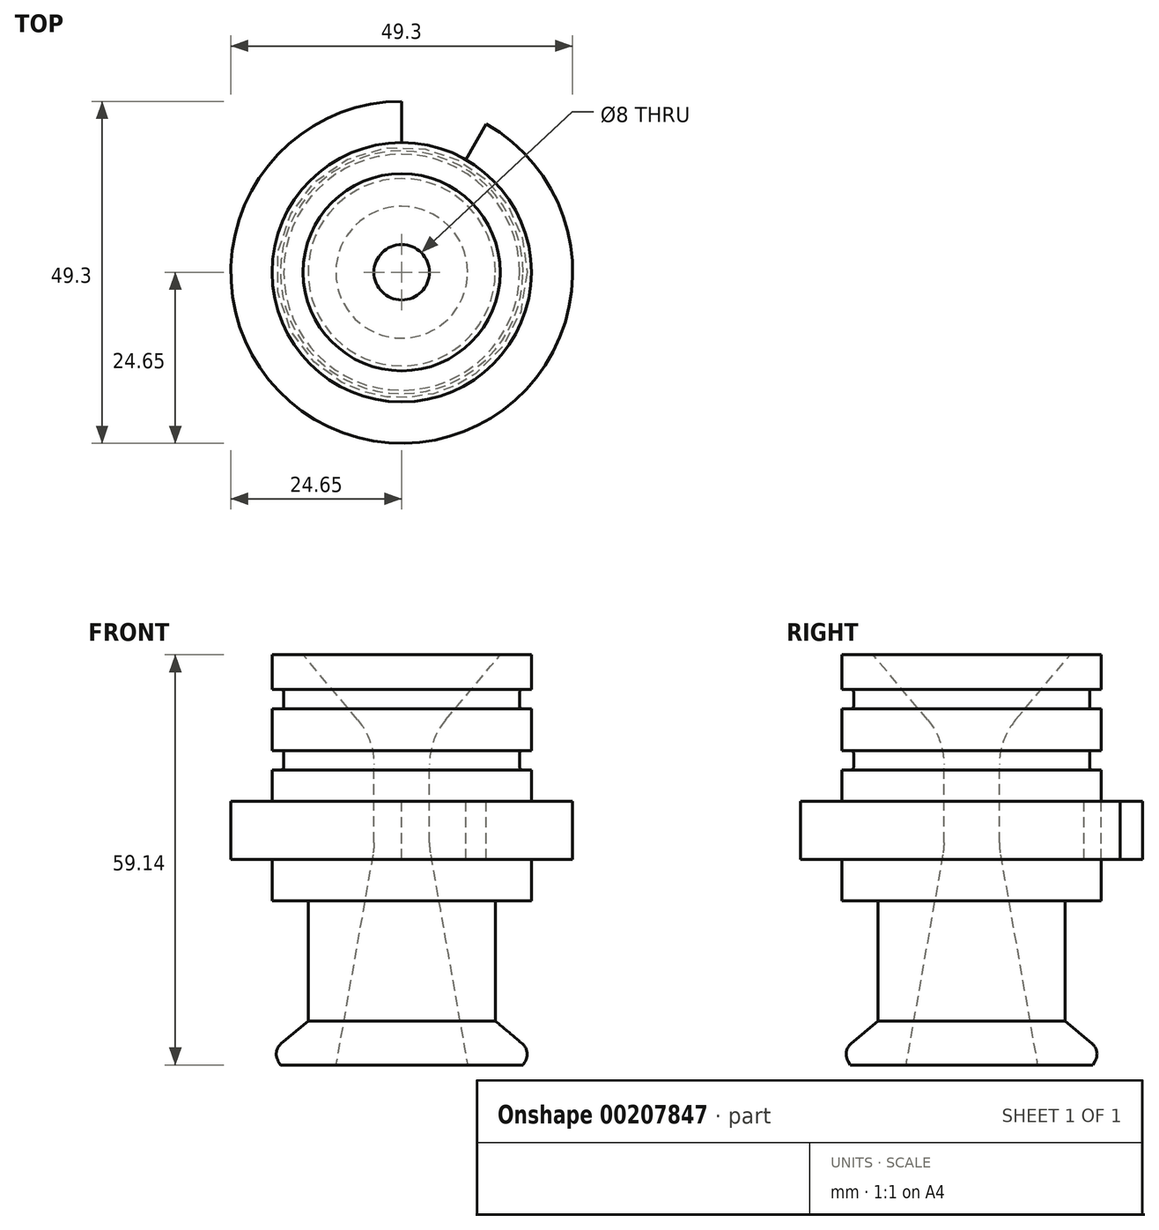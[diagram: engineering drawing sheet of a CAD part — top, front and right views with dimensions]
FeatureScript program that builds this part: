
annotation { "Feature Type Name" : "Feature", "Feature Type Description" : "" }
export const myFeature = defineFeature(function(context is Context, id is Id, definition is map)
    precondition{}
    {
        {
            var Q0;
            Q0=qCreatedBy(makeId("Front.planeOp"),FACE);
            var sketch = newSketch(context, id + "F0", { "sketchPlane" : qUnion([Q0])});
            skLineSegment(sketch, "E0", {"start": v(-18.7, 0) * mm, "end": v(-18.7, 6) * mm});
            skLineSegment(sketch, "E1", {"start": v(-18.7, 6) * mm, "end": v(-24.65, 6) * mm});
            skLineSegment(sketch, "E2", {"start": v(-24.65, 6) * mm, "end": v(-24.65, 14.4) * mm});
            skLineSegment(sketch, "E3", {"start": v(-18.7, 14.4) * mm, "end": v(-18.7, 18.9) * mm});
            skLineSegment(sketch, "E4", {"start": v(-18.7, 18.9) * mm, "end": v(-17.42, 18.9) * mm});
            skLineSegment(sketch, "E5", {"start": v(-17.02, 19.3) * mm, "end": v(-17.02, 21.3) * mm});
            skLineSegment(sketch, "E6", {"start": v(-17.42, 21.7) * mm, "end": v(-18.7, 21.7) * mm});
            skLineSegment(sketch, "E7", {"start": v(-18.7, 21.7) * mm, "end": v(-18.7, 27.7) * mm});
            skLineSegment(sketch, "E8", {"start": v(-18.7, 27.7) * mm, "end": v(-17.42, 27.7) * mm});
            skLineSegment(sketch, "E9", {"start": v(-17.02, 28.1) * mm, "end": v(-17.02, 30.1) * mm});
            skLineSegment(sketch, "E10", {"start": v(-17.42, 30.5) * mm, "end": v(-18.7, 30.5) * mm});
            skLineSegment(sketch, "E11", {"start": v(-18.7, 14.4) * mm, "end": v(-24.65, 14.4) * mm});
            skLineSegment(sketch, "E12", {"start": v(-14.22, 35.5) * mm, "end": v(-6.34, 26.11) * mm});
            skLineSegment(sketch, "E13", {"start": v(-4, 8.43) * mm, "end": v(-4, 19.68) * mm});
            skLineSegment(sketch, "E14", {"start": v(0, 48.19) * mm, "end": v(0, -42.57) * mm});
            skPoint(sketch, "E15.visualSharp", {"position": v(-4, 23.32) * mm});
            skArc(sketch, "E15.filletArc", {"start": v(-4, 19.68) * mm, "mid": v(-4.6, 23.1) * mm, "end": v(-6.34, 26.11) * mm});
            skPoint(sketch, "E16.visualSharp", {"position": v(-4, 7.32) * mm});
            skArc(sketch, "E16.filletArc", {"start": v(-4.15, 6.7) * mm, "mid": v(-4.04, 7.55) * mm, "end": v(-4, 8.43) * mm});
            skLineSegment(sketch, "E17", {"start": v(-18.7, 30.5) * mm, "end": v(-18.7, 35.5) * mm});
            skLineSegment(sketch, "E18", {"start": v(-18.7, 35.5) * mm, "end": v(-14.22, 35.5) * mm});
            skLineSegment(sketch, "E19", {"start": v(-4.15, 6.7) * mm, "end": v(-9.5, -23.64) * mm});
            skLineSegment(sketch, "E20", {"start": v(-13.5, 0) * mm, "end": v(-18.7, 0) * mm});
            skLineSegment(sketch, "E21", {"start": v(-17.5, -23.64) * mm, "end": v(-9.5, -23.64) * mm});
            skLineSegment(sketch, "E22", {"start": v(-17.5, -23.64) * mm, "end": v(-17.82, -23.08) * mm});
            skLineSegment(sketch, "E23", {"start": v(-17.38, -20.55) * mm, "end": v(-13.5, -17.3) * mm});
            skPoint(sketch, "E24.visualSharp", {"position": v(-18.66, -21.63) * mm});
            skArc(sketch, "E24.filletArc", {"start": v(-17.38, -20.55) * mm, "mid": v(-18.06, -21.74) * mm, "end": v(-17.82, -23.08) * mm});
            skLineSegment(sketch, "E25", {"start": v(-13.5, 0) * mm, "end": v(-13.5, -17.3) * mm});
            skPoint(sketch, "E26.visualSharp", {"position": v(-17.02, 30.5) * mm});
            skArc(sketch, "E26.filletArc", {"start": v(-17.02, 30.1) * mm, "mid": v(-17.14, 30.38) * mm, "end": v(-17.42, 30.5) * mm});
            skPoint(sketch, "E27.visualSharp", {"position": v(-17.02, 27.7) * mm});
            skArc(sketch, "E27.filletArc", {"start": v(-17.42, 27.7) * mm, "mid": v(-17.14, 27.82) * mm, "end": v(-17.02, 28.1) * mm});
            skPoint(sketch, "E28.visualSharp", {"position": v(-17.02, 21.7) * mm});
            skArc(sketch, "E28.filletArc", {"start": v(-17.02, 21.3) * mm, "mid": v(-17.14, 21.58) * mm, "end": v(-17.42, 21.7) * mm});
            skPoint(sketch, "E29.visualSharp", {"position": v(-17.02, 18.9) * mm});
            skArc(sketch, "E29.filletArc", {"start": v(-17.42, 18.9) * mm, "mid": v(-17.14, 19.02) * mm, "end": v(-17.02, 19.3) * mm});
            skSolve(sketch);
        }
        {
            var Q0;
            Q0=qSketchRegion(id+"F0",true);
            var Q1;
            Q1=sQuery(id+"F0.wireOp",EDGE,"E14");
            revolve(context, id + "F1", {"entities" : qUnion([Q0]), "axis" : qUnion([Q1]), "revolveType" : RevolveType.FULL});
        }
        {
            var Q0;
            Q0=makeQuery(id+"F1.opRevolve","SWEPT_FACE",FACE,{"disambiguationData":[OSD([sQuery(id+"F0.wireOp",EDGE,"E11")])]});
            var sketch = newSketch(context, id + "F2", { "sketchPlane" : qUnion([Q0])});
            skCircle(sketch, "E30.cCircle", {"center": v(0, 0) * mm, "radius": 18.7 * mm, "construction": true});
            skLineSegment(sketch, "E30.0", {"start": v(9.35, -16.2) * mm, "end": v(-9.35, -16.2) * mm});
            skLineSegment(sketch, "E30.1", {"start": v(-9.35, -16.2) * mm, "end": v(-18.7, 0) * mm});
            skLineSegment(sketch, "E30.2", {"start": v(-18.7, 0) * mm, "end": v(-9.35, 16.2) * mm});
            skLineSegment(sketch, "E30.3", {"start": v(-9.35, 16.2) * mm, "end": v(9.35, 16.2) * mm});
            skLineSegment(sketch, "E30.4", {"start": v(9.35, 16.2) * mm, "end": v(18.7, 0) * mm});
            skLineSegment(sketch, "E30.5", {"start": v(18.7, 0) * mm, "end": v(9.35, -16.2) * mm});
            skLineSegment(sketch, "E31.0", {"start": v(0, -18.7) * mm, "end": v(-16.2, -9.35) * mm});
            skLineSegment(sketch, "E31.1", {"start": v(-16.2, -9.35) * mm, "end": v(-16.2, 9.35) * mm});
            skLineSegment(sketch, "E31.2", {"start": v(-16.2, 9.35) * mm, "end": v(0, 18.7) * mm});
            skLineSegment(sketch, "E31.3", {"start": v(0, 18.7) * mm, "end": v(16.2, 9.35) * mm});
            skLineSegment(sketch, "E31.4", {"start": v(16.2, 9.35) * mm, "end": v(16.2, -9.35) * mm});
            skLineSegment(sketch, "E31.5", {"start": v(16.2, -9.35) * mm, "end": v(0, -18.7) * mm});
            skLineSegment(sketch, "E32", {"start": v(0, 18.7) * mm, "end": v(0, 24.65) * mm});
            skLineSegment(sketch, "E33", {"start": v(9.26, 16.24) * mm, "end": v(12.21, 21.41) * mm});
            skSolve(sketch);
        }
        {
            var Q0;
            {var subQ0=sQuery(id+"F2.wireOp",EDGE,"E32");Q0=makeQuery(id+"F2.imprint","IMPRINT",FACE,{"disambiguationData":[TD([[makeQuery(id+"F2.imprint","IMPRINT",EDGE,{"derivedFrom":subQ0}),-1.0]])]});}
            extrude(context, id + "F3", {"entities" : qUnion([Q0]), "operationType" : NewBodyOperationType.REMOVE, "endBound" : BoundingType.THROUGH_ALL, "oppositeDirection" : true, "depth" : 25 * mm});
        }
    });
